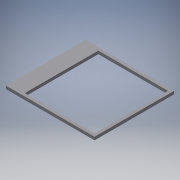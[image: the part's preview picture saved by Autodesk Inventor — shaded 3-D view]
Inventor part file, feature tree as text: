
AUTODESK INVENTOR PART (.ipt)
format: ipt  version: 2018.3 (Build 223284000, 284)  size: 105,472 bytes
history: native  units: mm
features: extrude x3, sketch x3
ambient origin geometry x8: Origin, YZ Plane, XZ Plane, XY Plane, X Axis, Y Axis, Z Axis, Center Point
bodies: Solid1 (feature_tree)
feature tree (6):
  extrude  "Extrusion1"  Depth=52.5mm
  extrude  "Extrusion2"  Depth=46.0mm
  extrude  "Extrusion3"  Depth=48.5mm TaperAngle=0.0deg
  sketch  "Sketch1"  dims[d0=50.0mm d1=52.5mm]
  sketch  "Sketch2"  dims[d2=2.0mm d3=0.0mm d4=46.0mm]
  sketch  "Sketch3"  dims[d5=48.5mm d6=10.0mm d7=0.0mm d8=8.5mm d9=0.0mm]
